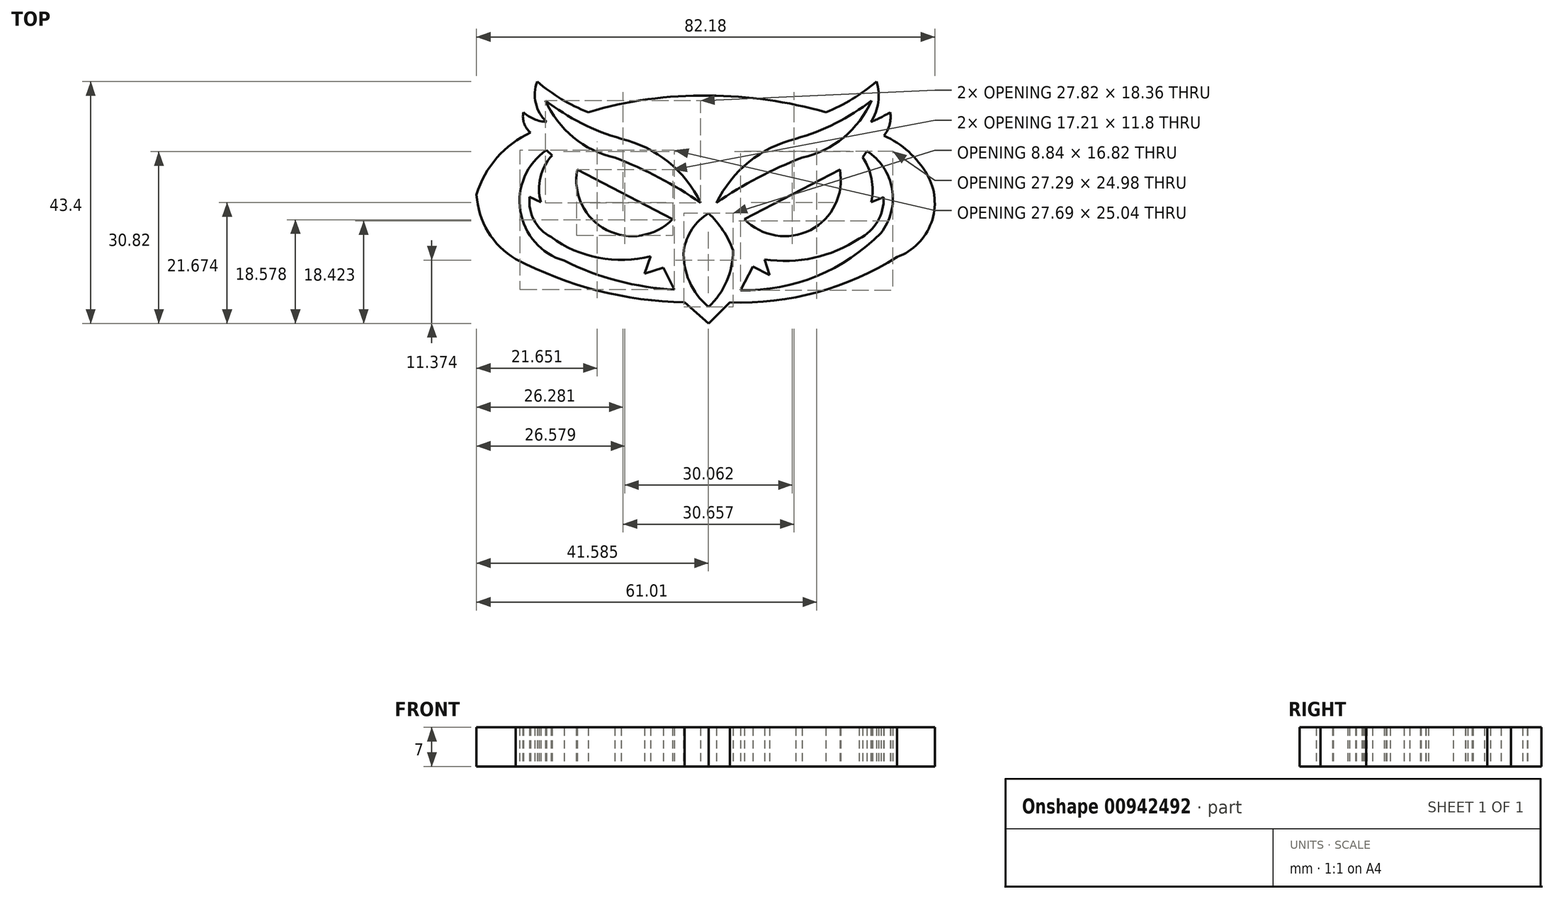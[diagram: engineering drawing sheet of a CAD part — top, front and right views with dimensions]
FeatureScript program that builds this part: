
annotation { "Feature Type Name" : "Feature", "Feature Type Description" : "" }
export const myFeature = defineFeature(function(context is Context, id is Id, definition is map)
    precondition{}
    {
        {
            var Q0;
            Q0=qCreatedBy(makeId("Top.planeOp"),FACE);
            var sketch = newSketch(context, id + "F0", { "sketchPlane" : qUnion([Q0])});
            skArc(sketch, "E0", {"start": v(-31.9, 21.13) * mm, "mid": v(-37.95, 16.61) * mm, "end": v(-41.6, 10) * mm});
            skArc(sketch, "E1", {"start": v(-41.6, 10) * mm, "mid": v(-39.55, 3.33) * mm, "end": v(-34.56, -1.56) * mm});
            skArc(sketch, "E2", {"start": v(-34.56, -1.56) * mm, "mid": v(-19.9, -7.22) * mm, "end": v(-4.32, -9.35) * mm});
            skLineSegment(sketch, "E3", {"start": v(-4.32, -9.35) * mm, "end": v(0, -13.12) * mm});
            skLineSegment(sketch, "E4", {"start": v(0, -13.12) * mm, "end": v(3.84, -9.35) * mm});
            skArc(sketch, "E5", {"start": v(3.84, -9.35) * mm, "mid": v(19.45, -7.54) * mm, "end": v(33.83, -1.19) * mm});
            skArc(sketch, "E6", {"start": v(33.83, -1.19) * mm, "mid": v(39.95, 4.95) * mm, "end": v(39.2, 13.59) * mm});
            skArc(sketch, "E7", {"start": v(39.2, 13.59) * mm, "mid": v(35.89, 17.69) * mm, "end": v(31.48, 20.58) * mm});
            skArc(sketch, "E8", {"start": v(31.48, 20.58) * mm, "mid": v(32.47, 22.56) * mm, "end": v(32.6, 24.78) * mm});
            skArc(sketch, "E9", {"start": v(29.13, 23.05) * mm, "mid": v(30.9, 23.84) * mm, "end": v(32.6, 24.78) * mm});
            skArc(sketch, "E10", {"start": v(29.13, 23.05) * mm, "mid": v(30.42, 26.56) * mm, "end": v(30.12, 30.28) * mm});
            skArc(sketch, "E11", {"start": v(21.03, 24.78) * mm, "mid": v(25.8, 27.16) * mm, "end": v(30.12, 30.28) * mm});
            skArc(sketch, "E12", {"start": v(21.03, 24.78) * mm, "mid": v(10.62, 27) * mm, "end": v(0, 27.75) * mm});
            skArc(sketch, "E13", {"start": v(0, 27.75) * mm, "mid": v(-10.9, 27.1) * mm, "end": v(-21.57, 24.78) * mm});
            skArc(sketch, "E14", {"start": v(-30.72, 30.28) * mm, "mid": v(-26.39, 27.14) * mm, "end": v(-21.57, 24.78) * mm});
            skArc(sketch, "E15", {"start": v(-30.72, 30.28) * mm, "mid": v(-31, 26.41) * mm, "end": v(-29.06, 23.05) * mm});
            skArc(sketch, "E16", {"start": v(-33.2, 24.78) * mm, "mid": v(-31.28, 23.54) * mm, "end": v(-29.06, 23.05) * mm});
            skArc(sketch, "E17", {"start": v(-33.2, 24.78) * mm, "mid": v(-33.08, 22.77) * mm, "end": v(-31.9, 21.13) * mm});
            skArc(sketch, "E18", {"start": v(-29.24, 26.88) * mm, "mid": v(-22.77, 22.79) * mm, "end": v(-15.64, 20.02) * mm});
            skArc(sketch, "E19", {"start": v(-1.42, 8.52) * mm, "mid": v(-7.24, 15.86) * mm, "end": v(-15.64, 20.02) * mm});
            skArc(sketch, "E20", {"start": v(-1.42, 8.52) * mm, "mid": v(-8.86, 13.05) * mm, "end": v(-16.81, 16.62) * mm});
            skArc(sketch, "E21", {"start": v(-29.24, 26.88) * mm, "mid": v(-24.25, 20.27) * mm, "end": v(-16.81, 16.62) * mm});
            skLineSegment(sketch, "E22", {"start": v(0, 0) * mm, "end": v(0, 6.66) * mm});
            skArc(sketch, "E23.MirrorCS", {"start": v(1.42, 8.52) * mm, "mid": v(7.24, 15.86) * mm, "end": v(15.64, 20.02) * mm});
            skArc(sketch, "E24.MirrorCS", {"start": v(1.42, 8.52) * mm, "mid": v(8.86, 13.05) * mm, "end": v(16.81, 16.62) * mm});
            skArc(sketch, "E25.MirrorCS", {"start": v(29.24, 26.88) * mm, "mid": v(24.25, 20.27) * mm, "end": v(16.81, 16.62) * mm});
            skArc(sketch, "E26.MirrorCS", {"start": v(29.24, 26.88) * mm, "mid": v(22.77, 22.79) * mm, "end": v(15.64, 20.02) * mm});
            skLineSegment(sketch, "E27", {"start": v(-23.55, 14.45) * mm, "end": v(-6.42, 5.61) * mm});
            skArc(sketch, "E28", {"start": v(-23.55, 14.45) * mm, "mid": v(-18.28, 3.65) * mm, "end": v(-6.42, 5.61) * mm});
            skArc(sketch, "E29", {"start": v(-14.99, 10.03) * mm, "mid": v(-14.02, 7.62) * mm, "end": v(-11.49, 8.23) * mm});
            skArc(sketch, "E30.MirrorCS", {"start": v(14.99, 10.03) * mm, "mid": v(14.02, 7.62) * mm, "end": v(11.49, 8.23) * mm});
            skLineSegment(sketch, "E31.MirrorCS", {"start": v(23.55, 14.45) * mm, "end": v(6.42, 5.61) * mm});
            skArc(sketch, "E32.MirrorCS", {"start": v(23.55, 14.45) * mm, "mid": v(18.28, 3.65) * mm, "end": v(6.42, 5.61) * mm});
            skLineSegment(sketch, "E33", {"start": v(0, -7.43) * mm, "end": v(0, 6.66) * mm});
            skArc(sketch, "E34", {"start": v(-29.06, 17.98) * mm, "mid": v(-33.75, 7.06) * mm, "end": v(-25.9, -1.87) * mm});
            skArc(sketch, "E35", {"start": v(-25.9, -1.87) * mm, "mid": v(-16.28, -5.48) * mm, "end": v(-6.12, -7.06) * mm});
            skLineSegment(sketch, "E36", {"start": v(-8.1, -3.1) * mm, "end": v(-6.12, -7.06) * mm});
            skLineSegment(sketch, "E37", {"start": v(-8.1, -3.1) * mm, "end": v(-11.5, -4.16) * mm});
            skLineSegment(sketch, "E38", {"start": v(-11.5, -4.16) * mm, "end": v(-10.38, -1.07) * mm});
            skArc(sketch, "E39", {"start": v(-28.25, 2.4) * mm, "mid": v(-19.7, -1.36) * mm, "end": v(-10.38, -1.07) * mm});
            skArc(sketch, "E40", {"start": v(-32.08, 9.57) * mm, "mid": v(-31.29, 5.38) * mm, "end": v(-28.25, 2.4) * mm});
            skLineSegment(sketch, "E41", {"start": v(-32.08, 9.57) * mm, "end": v(-30.1, 8.64) * mm});
            skArc(sketch, "E42", {"start": v(-28.07, 17.05) * mm, "mid": v(-30.16, 13.1) * mm, "end": v(-30.1, 8.64) * mm});
            skLineSegment(sketch, "E43", {"start": v(-29.06, 17.98) * mm, "end": v(-28.07, 17.05) * mm});
            skArc(sketch, "E44", {"start": v(30.92, 3.14) * mm, "mid": v(32.9, 11.03) * mm, "end": v(28.39, 17.8) * mm});
            skArc(sketch, "E45", {"start": v(5.76, -7.19) * mm, "mid": v(19.4, -4.62) * mm, "end": v(30.92, 3.14) * mm});
            skLineSegment(sketch, "E46", {"start": v(5.76, -7.19) * mm, "end": v(7.98, -2.92) * mm});
            skLineSegment(sketch, "E47", {"start": v(7.98, -2.92) * mm, "end": v(10.92, -4.45) * mm});
            skLineSegment(sketch, "E48", {"start": v(10.92, -4.45) * mm, "end": v(10.02, -1.62) * mm});
            skArc(sketch, "E49", {"start": v(10.02, -1.62) * mm, "mid": v(18.87, -1.35) * mm, "end": v(27.03, 2.09) * mm});
            skArc(sketch, "E50", {"start": v(27.03, 2.09) * mm, "mid": v(30.3, 5.16) * mm, "end": v(31.42, 9.5) * mm});
            skLineSegment(sketch, "E51", {"start": v(31.42, 9.5) * mm, "end": v(29.2, 8.64) * mm});
            skArc(sketch, "E52", {"start": v(29.2, 8.64) * mm, "mid": v(29.23, 12.82) * mm, "end": v(27.64, 16.68) * mm});
            skLineSegment(sketch, "E53", {"start": v(27.64, 16.68) * mm, "end": v(28.39, 17.8) * mm});
            skArc(sketch, "E54", {"start": v(-4.45, 0) * mm, "mid": v(-3.44, -5.6) * mm, "end": v(0, -10.15) * mm});
            skArc(sketch, "E55", {"start": v(0, 6.66) * mm, "mid": v(-2.93, 3.8) * mm, "end": v(-4.45, 0) * mm});
            skArc(sketch, "E56", {"start": v(4.4, 0) * mm, "mid": v(2.58, 3.58) * mm, "end": v(0, 6.66) * mm});
            skArc(sketch, "E57", {"start": v(0, -10.15) * mm, "mid": v(3.27, -5.54) * mm, "end": v(4.4, 0) * mm});
            skSolve(sketch);
        }
        {
            var Q0;
            Q0 = qSketchRegion(id + "F0", true);
            extrude(context, id + "F1", {"entities" : qUnion([Q0]), "depth" : 7 * mm, "offsetDistance" : 25 * mm});
        }
    });
